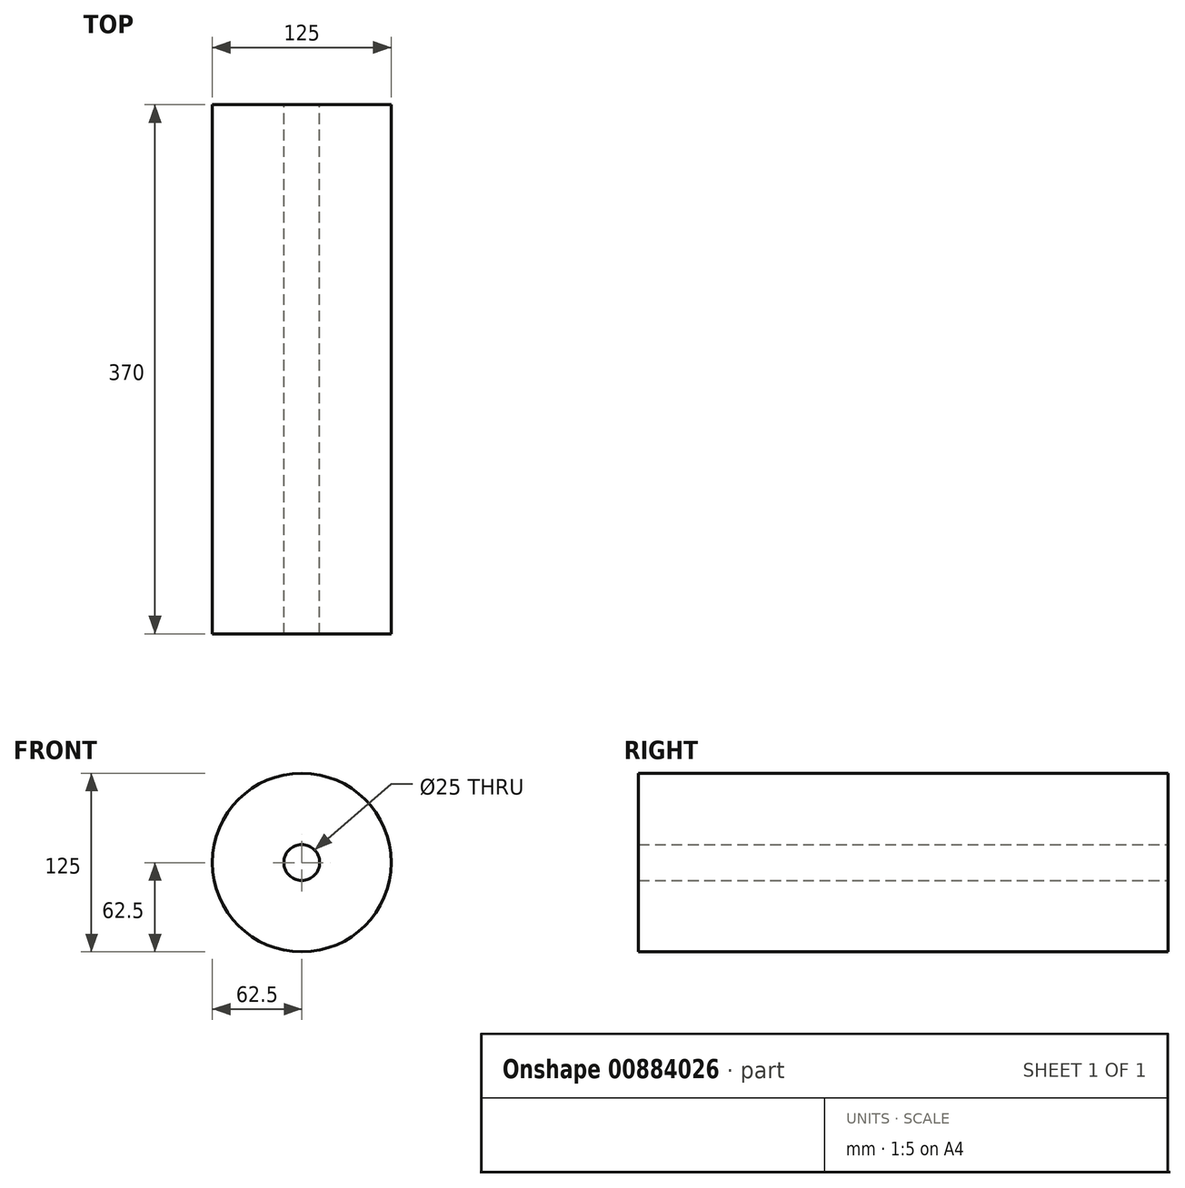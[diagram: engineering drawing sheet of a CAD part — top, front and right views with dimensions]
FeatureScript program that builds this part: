
annotation { "Feature Type Name" : "Feature", "Feature Type Description" : "" }
export const myFeature = defineFeature(function(context is Context, id is Id, definition is map)
    precondition{}
    {
        {
            var Q0;
            Q0=qCreatedBy(makeId("Front.planeOp"),FACE);
            var sketch = newSketch(context, id + "F0", { "sketchPlane" : qUnion([Q0])});
            skCircle(sketch, "E0", {"center": v(0, 0) * mm, "radius": 120 * mm});
            skCircle(sketch, "E1", {"center": v(0, 0) * mm, "radius": 12.5 * mm});
            skCircle(sketch, "E2", {"center": v(0, 0) * mm, "radius": 62.5 * mm});
            skSolve(sketch);
        }
        {
            var Q0;
            Q0=makeQuery(id+"F0.imprint","IMPRINT",FACE,{"disambiguationData":[TD([[makeQuery(id+"F0.imprint","IMPRINT",EDGE,{"derivedFrom":sQuery(id+"F0.wireOp",EDGE,"E1")}),-1.0]])]});
            extrude(context, id + "F1", {"entities" : qUnion([Q0]), "depth" : 370 * mm, "offsetDistance" : 25.4 * mm});
        }
    });
